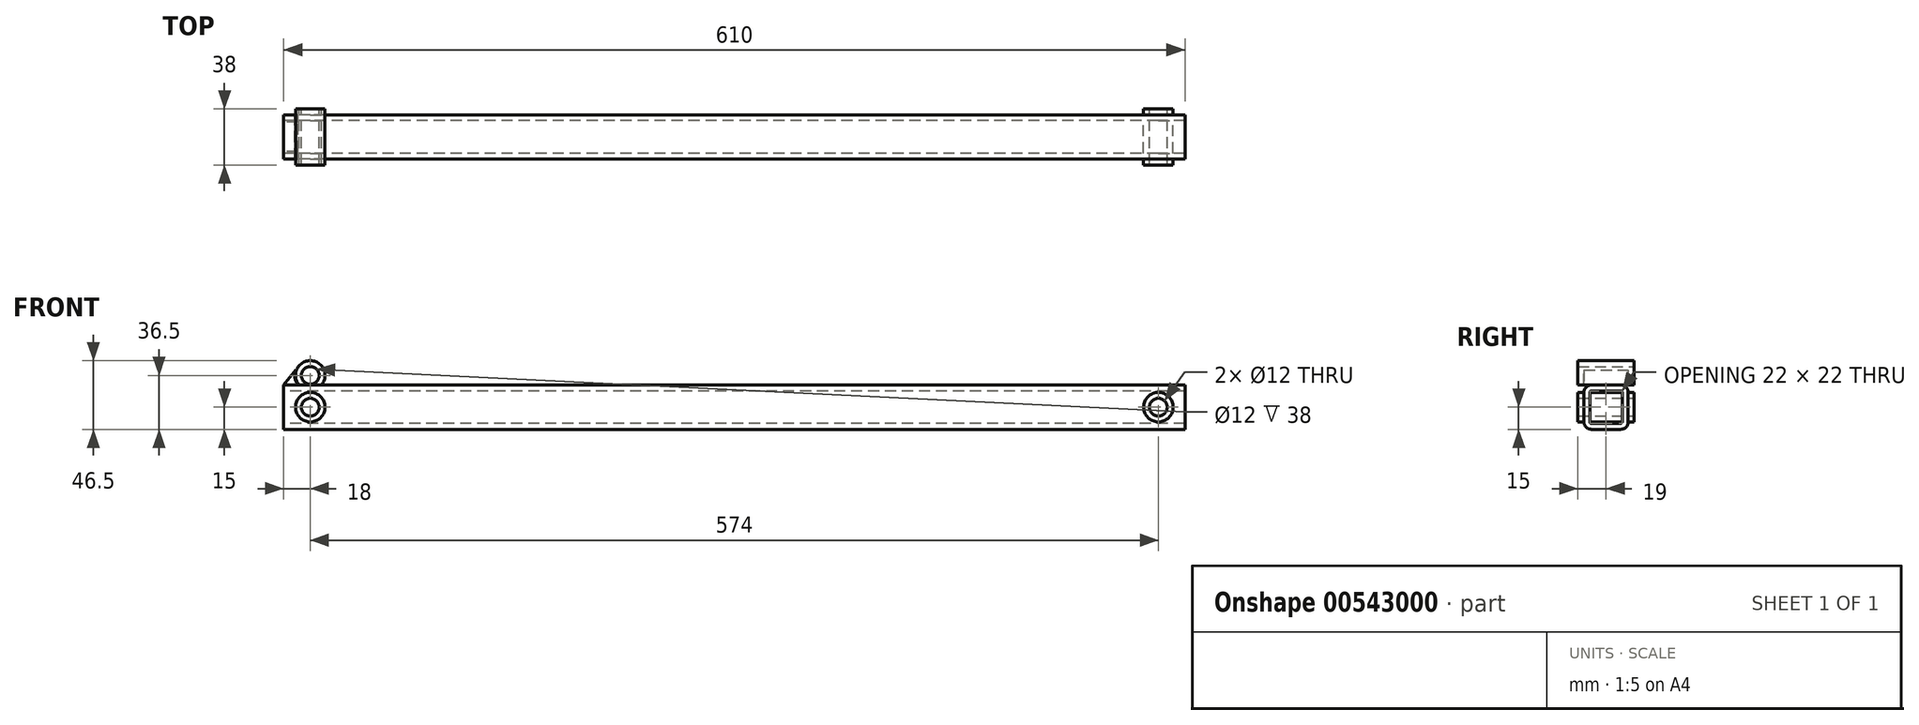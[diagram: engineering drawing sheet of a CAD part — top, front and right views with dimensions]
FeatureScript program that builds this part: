
annotation { "Feature Type Name" : "Feature", "Feature Type Description" : "" }
export const myFeature = defineFeature(function(context is Context, id is Id, definition is map)
    precondition{}
    {
        {
            var Q0;
            Q0=qCreatedBy(makeId("Right.planeOp"),FACE);
            var sketch = newSketch(context, id + "F0", { "sketchPlane" : qUnion([Q0])});
            skLineSegment(sketch, "E0", {"start": v(0, 5) * mm, "end": v(0, 25) * mm});
            skLineSegment(sketch, "E1", {"start": v(-5, 30) * mm, "end": v(-25, 30) * mm});
            skLineSegment(sketch, "E2", {"start": v(-30, 25) * mm, "end": v(-30, 5) * mm});
            skLineSegment(sketch, "E3", {"start": v(-25, 0) * mm, "end": v(-5, 0) * mm});
            skPoint(sketch, "E4.visualSharp", {"position": v(-30, 30) * mm});
            skArc(sketch, "E4.filletArc", {"start": v(-25, 30) * mm, "mid": v(-28.54, 28.54) * mm, "end": v(-30, 25) * mm});
            skPoint(sketch, "E5.visualSharp", {"position": v(0, 30) * mm});
            skArc(sketch, "E5.filletArc", {"start": v(0, 25) * mm, "mid": v(-1.46, 28.54) * mm, "end": v(-5, 30) * mm});
            skPoint(sketch, "E6.visualSharp", {"position": v(-30, 0) * mm});
            skArc(sketch, "E6.filletArc", {"start": v(-30, 5) * mm, "mid": v(-28.54, 1.46) * mm, "end": v(-25, 0) * mm});
            skPoint(sketch, "E7.visualSharp", {"position": v(0, 0) * mm});
            skArc(sketch, "E7.filletArc", {"start": v(-5, 0) * mm, "mid": v(-1.46, 1.46) * mm, "end": v(0, 5) * mm});
            skArc(sketch, "E8.0", {"start": v(-25, 26) * mm, "mid": v(-25.7, 25.7) * mm, "end": v(-26, 25) * mm});
            skLineSegment(sketch, "E8.1", {"start": v(-5, 26) * mm, "end": v(-25, 26) * mm});
            skLineSegment(sketch, "E8.2", {"start": v(-26, 25) * mm, "end": v(-26, 5) * mm});
            skArc(sketch, "E8.3", {"start": v(-4, 25) * mm, "mid": v(-4.3, 25.7) * mm, "end": v(-5, 26) * mm});
            skArc(sketch, "E8.4", {"start": v(-26, 5) * mm, "mid": v(-25.7, 4.3) * mm, "end": v(-25, 4) * mm});
            skLineSegment(sketch, "E8.5", {"start": v(-25, 4) * mm, "end": v(-5, 4) * mm});
            skArc(sketch, "E8.6", {"start": v(-5, 4) * mm, "mid": v(-4.3, 4.3) * mm, "end": v(-4, 5) * mm});
            skLineSegment(sketch, "E8.7", {"start": v(-4, 5) * mm, "end": v(-4, 25) * mm});
            skSolve(sketch);
        }
        {
            var Q0;
            Q0=makeQuery(id+"F0.imprint","IMPRINT",FACE,{"disambiguationData":[TD([[makeQuery(id+"F0.imprint","IMPRINT",EDGE,{"derivedFrom":sQuery(id+"F0.wireOp",EDGE,"E0")}),1.0]])]});
            extrude(context, id + "F1", {"entities" : qUnion([Q0]), "flatOperationType" : FlatOperationType.REMOVE, "depth" : 610 * mm, "offsetDistance" : 25 * mm, "domain" : OperationDomain.MODEL});
        }
        {
            var Q0;
            Q0=qCreatedBy(makeId("Front.planeOp"),FACE);
            var sketch = newSketch(context, id + "F2", { "sketchPlane" : qUnion([Q0])});
            skLineSegment(sketch, "E9.0", {"start": v(0, 5) * mm, "end": v(0, 25) * mm, "construction": true});
            skLineSegment(sketch, "E10", {"start": v(0, 15) * mm, "end": v(18, 15) * mm, "construction": true});
            skPoint(sketch, "E10.endSnap0", {"position": v(0, 15) * mm});
            skCircle(sketch, "E11", {"center": v(18, 15) * mm, "radius": 6 * mm});
            skCircle(sketch, "E12.0", {"center": v(18, 15) * mm, "radius": 10 * mm});
            skLineSegment(sketch, "E13.0", {"start": v(610, 5) * mm, "end": v(610, 25) * mm});
            skLineSegment(sketch, "E14", {"start": v(610, 15) * mm, "end": v(592, 15) * mm, "construction": true});
            skCircle(sketch, "E15", {"center": v(592, 15) * mm, "radius": 6 * mm});
            skCircle(sketch, "E16.0", {"center": v(592, 15) * mm, "radius": 10 * mm});
            skLineSegment(sketch, "E17", {"start": v(18, 15) * mm, "end": v(18, 36.5) * mm, "construction": true});
            skCircle(sketch, "E18", {"center": v(18, 36.5) * mm, "radius": 6 * mm});
            skCircle(sketch, "E19.0", {"center": v(18, 36.5) * mm, "radius": 10 * mm});
            skPoint(sketch, "E20.0", {"position": v(0, 30) * mm});
            skLineSegment(sketch, "E21.0", {"start": v(610, 30) * mm, "end": v(0, 30) * mm});
            skLineSegment(sketch, "E22", {"start": v(0, 30) * mm, "end": v(8.13, 40.17) * mm});
            skLineSegment(sketch, "E23", {"start": v(18, 15) * mm, "end": v(36, 15) * mm, "construction": true});
            skLineSegment(sketch, "E24", {"start": v(36, 15) * mm, "end": v(36, 32.63) * mm, "construction": true});
            skLineSegment(sketch, "E25", {"start": v(0, 30) * mm, "end": v(36, 30) * mm});
            skLineSegment(sketch, "E26", {"start": v(36, 30) * mm, "end": v(25.81, 42.74) * mm});
            skArc(sketch, "E27", {"start": v(8.13, 40.17) * mm, "mid": v(18, 25.97) * mm, "end": v(27.87, 40.17) * mm});
            skSolve(sketch);
        }
        {
            var Q0;
            Q0=makeQuery(id+"F2.imprint","IMPRINT",FACE,{"disambiguationData":[TD([[makeQuery(id+"F2.imprint","IMPRINT",EDGE,{"derivedFrom":sQuery(id+"F2.wireOp",EDGE,"E15")}),1.0]])]});
            var Q1;
            Q1=makeQuery(id+"F2.imprint","IMPRINT",FACE,{"disambiguationData":[TD([[makeQuery(id+"F2.imprint","IMPRINT",EDGE,{"derivedFrom":sQuery(id+"F2.wireOp",EDGE,"E11")}),1.0]])]});
            extrude(context, id + "F3", {"entities" : qUnion([Q0, Q1]), "operationType" : NewBodyOperationType.REMOVE, "endBound" : BoundingType.THROUGH_ALL, "depth" : 38.9 * mm, "offsetDistance" : 25 * mm});
        }
        {
            var Q0;
            Q0=makeQuery(id+"F2.imprint","IMPRINT",FACE,{"disambiguationData":[TD([[makeQuery(id+"F2.imprint","IMPRINT",EDGE,{"derivedFrom":sQuery(id+"F2.wireOp",EDGE,"E15")}),-1.0]])]});
            var Q1;
            Q1=makeQuery(id+"F2.imprint","IMPRINT",FACE,{"disambiguationData":[TD([[makeQuery(id+"F2.imprint","IMPRINT",EDGE,{"derivedFrom":sQuery(id+"F2.wireOp",EDGE,"E11")}),-1.0]])]});
            extrude(context, id + "F4", {"entities" : qUnion([Q0, Q1]), "operationType" : NewBodyOperationType.ADD, "depth" : 34 * mm, "offsetDistance" : 25 * mm});
        }
        {
            var Q0;
            Q0=makeQuery(id+"F2.imprint","IMPRINT",FACE,{"disambiguationData":[TD([[makeQuery(id+"F2.imprint","IMPRINT",EDGE,{"derivedFrom":sQuery(id+"F2.wireOp",EDGE,"E15")}),-1.0]])]});
            var Q1;
            Q1=makeQuery(id+"F2.imprint","IMPRINT",FACE,{"disambiguationData":[TD([[makeQuery(id+"F2.imprint","IMPRINT",EDGE,{"derivedFrom":sQuery(id+"F2.wireOp",EDGE,"E11")}),-1.0]])]});
            extrude(context, id + "F5", {"entities" : qUnion([Q0, Q1]), "operationType" : NewBodyOperationType.ADD, "oppositeDirection" : true, "depth" : 4 * mm, "offsetDistance" : 25 * mm});
        }
        {
            var Q0;
            Q0=makeQuery(id+"F2.imprint","IMPRINT",FACE,{"disambiguationData":[TD([[makeQuery(id+"F2.imprint","IMPRINT",EDGE,{"derivedFrom":sQuery(id+"F2.wireOp",EDGE,"E22")}),-1.0]])]});
            extrude(context, id + "F6", {"entities" : qUnion([Q0]), "operationType" : NewBodyOperationType.ADD, "depth" : 30 * mm, "offsetDistance" : 25 * mm});
        }
        {
            var Q0;
            Q0=makeQuery(id+"F2.imprint","IMPRINT",FACE,{"disambiguationData":[TD([[makeQuery(id+"F2.imprint","IMPRINT",EDGE,{"derivedFrom":sQuery(id+"F2.wireOp",EDGE,"E18")}),-1.0]])]});
            extrude(context, id + "F7", {"entities" : qUnion([Q0]), "flatOperationType" : FlatOperationType.REMOVE, "depth" : 34 * mm, "offsetDistance" : 25 * mm, "domain" : OperationDomain.MODEL});
        }
        {
            var Q0;
            Q0=makeQuery(id+"F2.imprint","IMPRINT",FACE,{"disambiguationData":[TD([[makeQuery(id+"F2.imprint","IMPRINT",EDGE,{"derivedFrom":sQuery(id+"F2.wireOp",EDGE,"E18")}),-1.0]])]});
            extrude(context, id + "F8", {"entities" : qUnion([Q0]), "operationType" : NewBodyOperationType.ADD, "oppositeDirection" : true, "depth" : 4 * mm, "offsetDistance" : 25 * mm});
        }
    });
